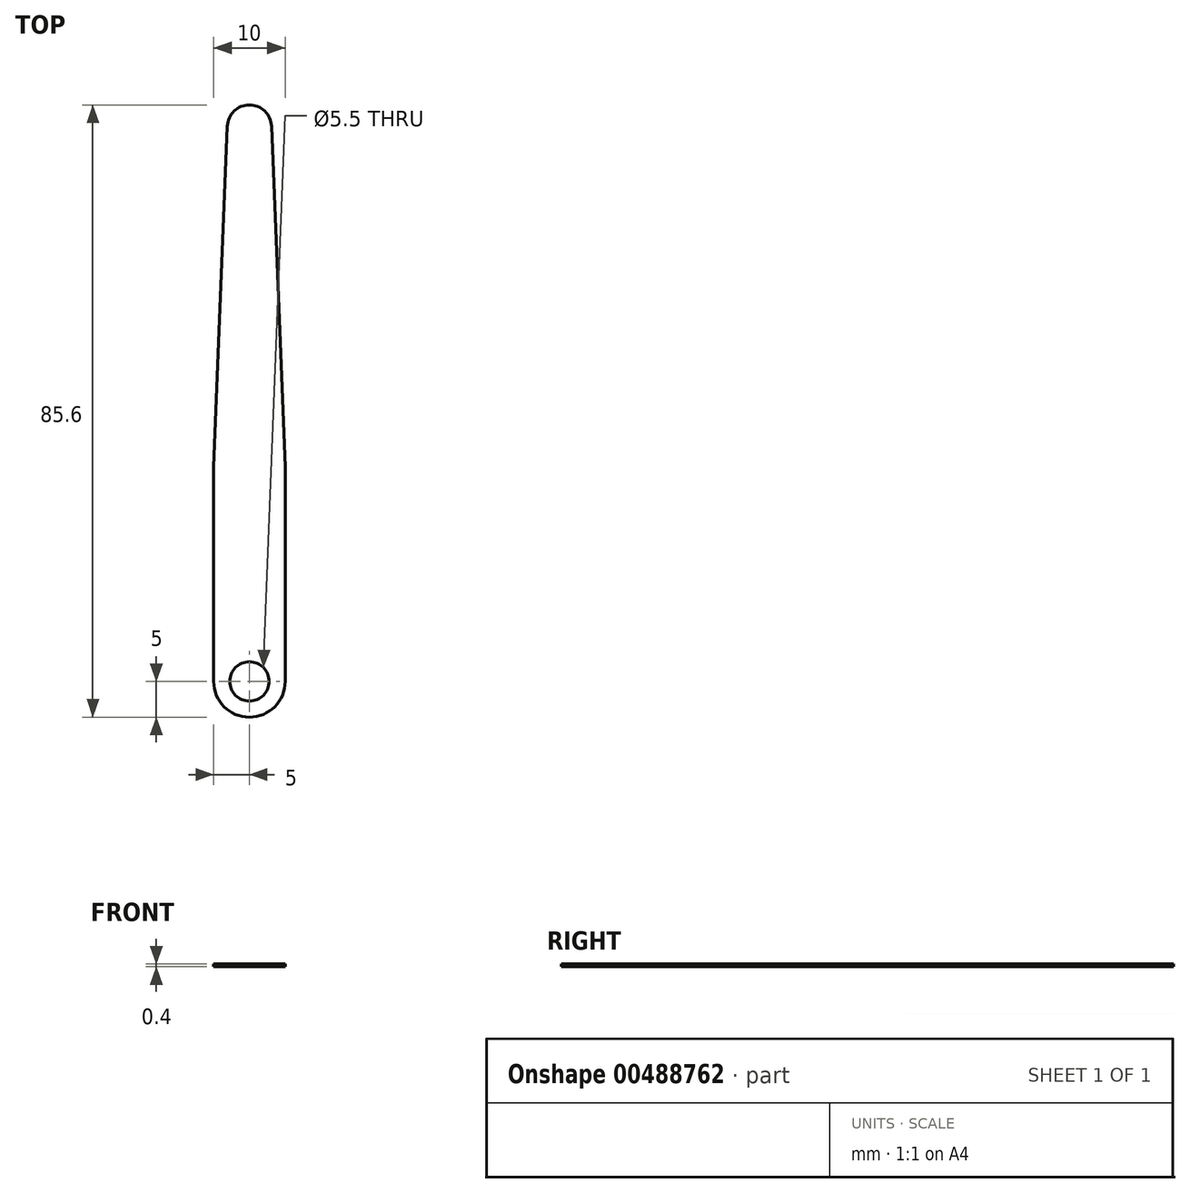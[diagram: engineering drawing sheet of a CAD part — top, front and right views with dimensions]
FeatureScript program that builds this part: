
annotation { "Feature Type Name" : "Feature", "Feature Type Description" : "" }
export const myFeature = defineFeature(function(context is Context, id is Id, definition is map)
    precondition{}
    {
        {
            var Q0;
            Q0=qCreatedBy(makeId("Top.planeOp"),FACE);
            var sketch = newSketch(context, id + "F0", { "sketchPlane" : qUnion([Q0])});
            skArc(sketch, "E0", {"start": v(-5, 0) * mm, "mid": v(0, -5) * mm, "end": v(5, 0) * mm});
            skCircle(sketch, "E1", {"center": v(0, 0) * mm, "radius": 2.75 * mm});
            skLineSegment(sketch, "E2.left", {"start": v(-5, 0) * mm, "end": v(-5, 30) * mm});
            skLineSegment(sketch, "E2.right", {"start": v(5, 0) * mm, "end": v(5, 30) * mm});
            skLineSegment(sketch, "E3", {"start": v(-5, 30) * mm, "end": v(-3.1, 77.62) * mm});
            skArc(sketch, "E4", {"start": v(3.1, 77.62) * mm, "mid": v(0, 80.6) * mm, "end": v(-3.1, 77.62) * mm});
            skPoint(sketch, "E5.center.orphan", {"position": v(0, 92.5) * mm});
            skPoint(sketch, "E6.center.orphan", {"position": v(0, 62.5) * mm});
            skLineSegment(sketch, "E7", {"start": v(5, 30) * mm, "end": v(3.1, 77.62) * mm});
            skSolve(sketch);
        }
        {
            var Q0;
            Q0=makeQuery(id+"F0.imprint","IMPRINT",FACE,{"disambiguationData":[TD([[makeQuery(id+"F0.imprint","IMPRINT",EDGE,{"derivedFrom":sQuery(id+"F0.wireOp",EDGE,"E0")}),1.0]])]});
            extrude(context, id + "F1", {"entities" : qUnion([Q0]), "depth" : 0.4 * mm, "offsetDistance" : 25 * mm});
        }
    });
